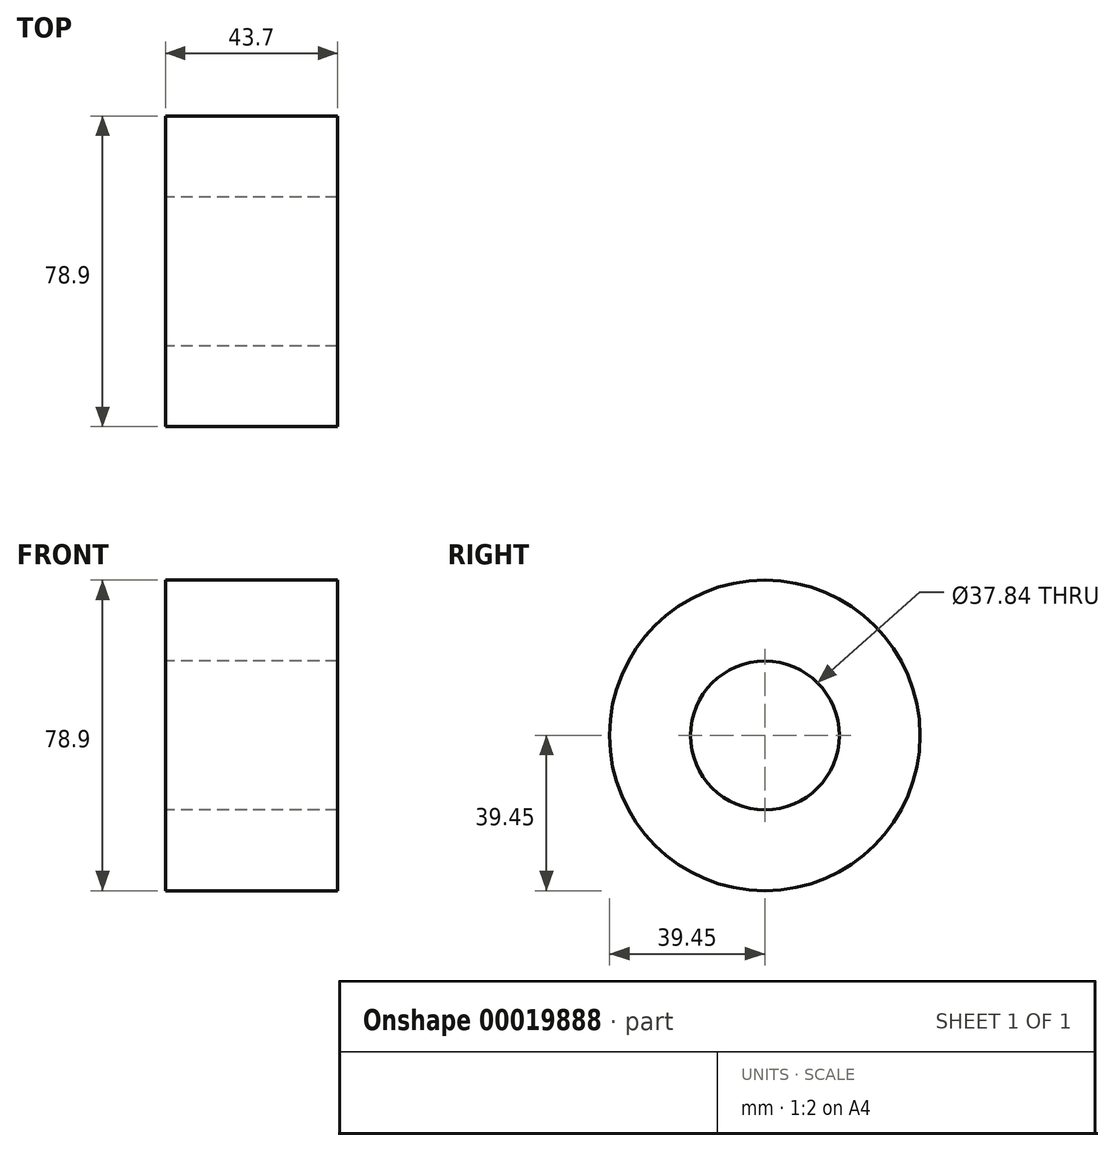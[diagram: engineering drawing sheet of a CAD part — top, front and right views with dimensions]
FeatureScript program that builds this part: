
annotation { "Feature Type Name" : "Feature", "Feature Type Description" : "" }
export const myFeature = defineFeature(function(context is Context, id is Id, definition is map)
    precondition{}
    {
        {
            var Q0;
            Q0=qCreatedBy(makeId("Front.planeOp"),FACE);
            var sketch = newSketch(context, id + "F0", { "sketchPlane" : qUnion([Q0])});
            skLineSegment(sketch, "E0", {"start": v(-66.72, 0) * mm, "end": v(55.29, 0) * mm});
            skLineSegment(sketch, "E1.bottom", {"start": v(-23.32, 39.45) * mm, "end": v(20.38, 39.45) * mm});
            skLineSegment(sketch, "E1.top", {"start": v(-23.32, 18.92) * mm, "end": v(20.38, 18.92) * mm});
            skLineSegment(sketch, "E1.left", {"start": v(-23.32, 39.45) * mm, "end": v(-23.32, 18.92) * mm});
            skLineSegment(sketch, "E1.right", {"start": v(20.38, 39.45) * mm, "end": v(20.38, 18.92) * mm});
            skSolve(sketch);
        }
        {
            var Q0;
            Q0=makeQuery(id+"F0.imprint","IMPRINT",FACE,{"disambiguationData":[TD([[makeQuery(id+"F0.imprint","IMPRINT",EDGE,{"derivedFrom":sQuery(id+"F0.wireOp",EDGE,"E1.bottom")}),-1.0]])]});
            var Q1;
            Q1=sQuery(id+"F0.wireOp",EDGE,"E0");
            revolve(context, id + "F1", {"entities" : qUnion([Q0]), "axis" : qUnion([Q1]), "revolveType" : RevolveType.FULL});
        }
    });
